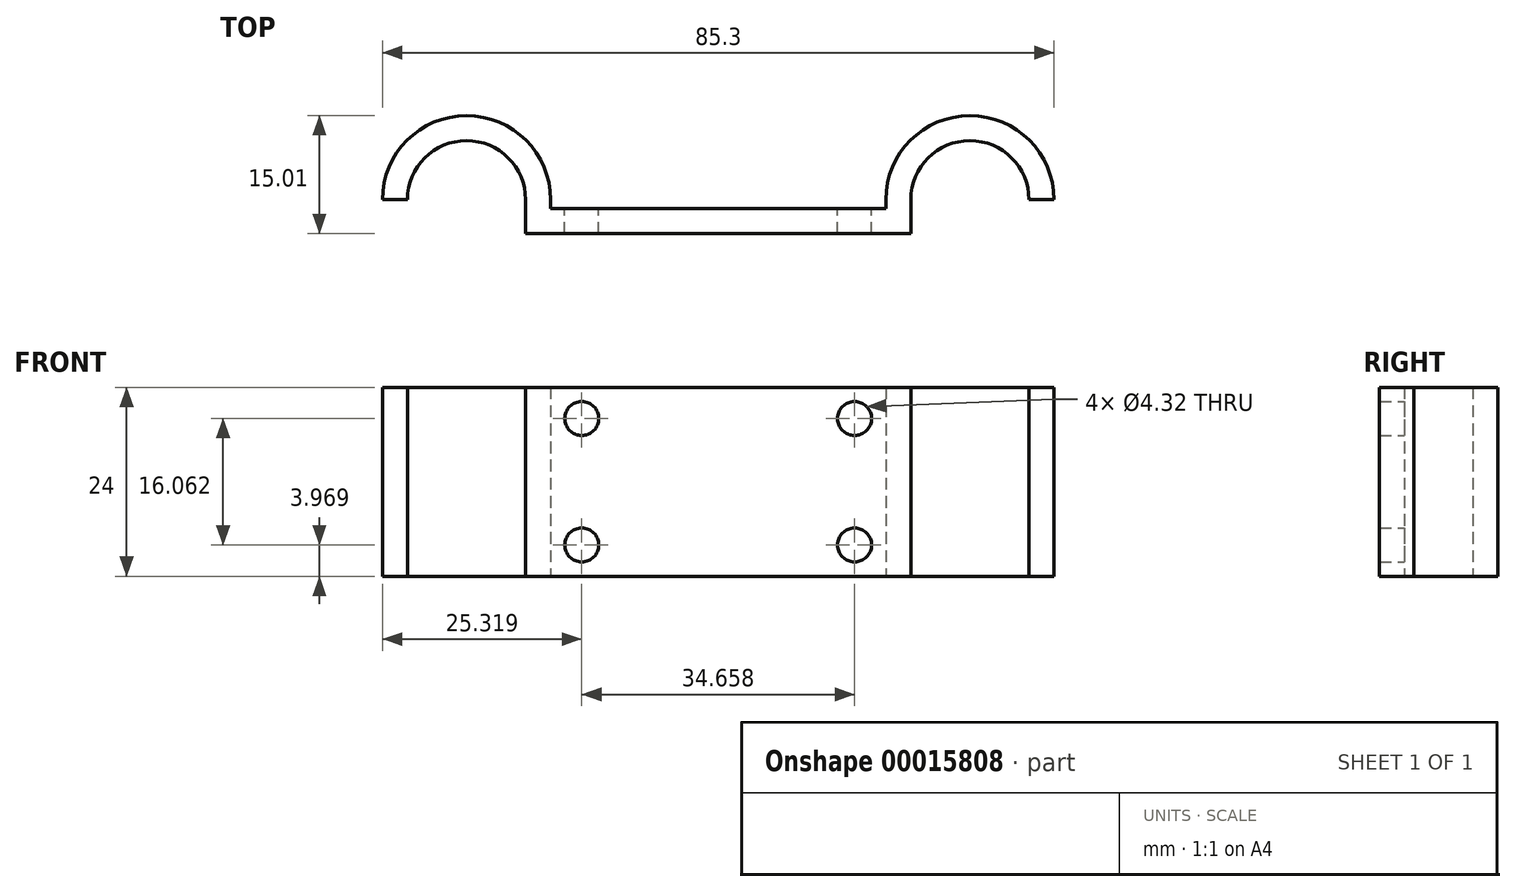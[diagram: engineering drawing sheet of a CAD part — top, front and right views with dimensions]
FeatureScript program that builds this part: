
annotation { "Feature Type Name" : "Feature", "Feature Type Description" : "" }
export const myFeature = defineFeature(function(context is Context, id is Id, definition is map)
    precondition{}
    {
        {
            var Q0;
            Q0=qCreatedBy(makeId("Top.planeOp"),FACE);
            var sketch = newSketch(context, id + "F0", { "sketchPlane" : qUnion([Q0])});
            skLineSegment(sketch, "E0.bottom", {"start": v(0, 0) * mm, "end": v(42.6, 0) * mm});
            skLineSegment(sketch, "E0.top", {"start": v(-3.17, -3.17) * mm, "end": v(45.77, -3.17) * mm});
            skLineSegment(sketch, "E1", {"start": v(21.3, 0) * mm, "end": v(21.3, -3.17) * mm});
            skLineSegment(sketch, "E2", {"start": v(0, 0) * mm, "end": v(0, 1.15) * mm});
            skLineSegment(sketch, "E3", {"start": v(-3.17, -3.17) * mm, "end": v(-3.17, 1.15) * mm});
            skLineSegment(sketch, "E4", {"start": v(42.6, 0) * mm, "end": v(42.6, 1.15) * mm});
            skLineSegment(sketch, "E5", {"start": v(45.77, -3.17) * mm, "end": v(45.77, 1.15) * mm});
            skLineSegment(sketch, "E6", {"start": v(0, 1.15) * mm, "end": v(-3.17, 1.15) * mm});
            skLineSegment(sketch, "E7", {"start": v(42.6, 1.15) * mm, "end": v(45.77, 1.15) * mm});
            skArc(sketch, "E8", {"start": v(-3.18, 1.15) * mm, "mid": v(-10.68, 8.65) * mm, "end": v(-18.18, 1.15) * mm});
            skArc(sketch, "E9", {"start": v(0, 1.15) * mm, "mid": v(-10.67, 11.83) * mm, "end": v(-21.35, 1.15) * mm});
            skArc(sketch, "E10", {"start": v(63.95, 1.15) * mm, "mid": v(53.27, 11.83) * mm, "end": v(42.6, 1.15) * mm});
            skArc(sketch, "E11", {"start": v(60.77, 1.15) * mm, "mid": v(53.27, 8.65) * mm, "end": v(45.77, 1.15) * mm});
            skLineSegment(sketch, "E12", {"start": v(-3.17, 1.15) * mm, "end": v(-18.18, 1.15) * mm, "construction": true});
            skLineSegment(sketch, "E13", {"start": v(-18.17, 1.15) * mm, "end": v(-21.35, 1.15) * mm});
            skLineSegment(sketch, "E14", {"start": v(45.77, 1.15) * mm, "end": v(60.77, 1.15) * mm, "construction": true});
            skLineSegment(sketch, "E15", {"start": v(60.77, 1.15) * mm, "end": v(63.95, 1.15) * mm});
            skSolve(sketch);
        }
        {
            var Q0;
            Q0 = qSketchRegion(id + "F0", true);
            extrude(context, id + "F1", {"entities" : qUnion([Q0]), "depth" : 24 * mm});
        }
        {
            var Q0;
            Q0=makeQuery(id+"F1.opExtrude","SWEPT_FACE",FACE,{"disambiguationData":[OSD([sQuery(id+"F0.wireOp",EDGE,"E0.bottom")])]});
            var sketch = newSketch(context, id + "F2", { "sketchPlane" : qUnion([Q0])});
            skLineSegment(sketch, "E16", {"start": v(-21.3, 0) * mm, "end": v(-21.3, 24) * mm, "construction": true});
            skLineSegment(sketch, "E17.rect.bottom", {"start": v(-38.63, 3.97) * mm, "end": v(-3.97, 3.97) * mm, "construction": true});
            skLineSegment(sketch, "E17.rect.top", {"start": v(-38.63, 20.03) * mm, "end": v(-3.97, 20.03) * mm, "construction": true});
            skLineSegment(sketch, "E17.rect.left", {"start": v(-38.63, 3.97) * mm, "end": v(-38.63, 20.03) * mm, "construction": true});
            skLineSegment(sketch, "E17.rect.right", {"start": v(-3.97, 3.97) * mm, "end": v(-3.97, 20.03) * mm, "construction": true});
            skPoint(sketch, "E17.rect.middle", {"position": v(-21.3, 12) * mm});
            skLineSegment(sketch, "E18.bottom", {"start": v(-38.63, 3.97) * mm, "end": v(-42.6, 3.97) * mm, "construction": true});
            skLineSegment(sketch, "E18.left", {"start": v(-38.63, 3.97) * mm, "end": v(-38.63, 0) * mm, "construction": true});
            skCircle(sketch, "E19", {"center": v(-38.63, 3.97) * mm, "radius": 2.16 * mm});
            skCircle(sketch, "E20", {"center": v(-38.63, 20.03) * mm, "radius": 2.16 * mm});
            skCircle(sketch, "E21", {"center": v(-3.97, 20.03) * mm, "radius": 2.16 * mm});
            skCircle(sketch, "E22", {"center": v(-3.97, 3.97) * mm, "radius": 2.16 * mm});
            skSolve(sketch);
        }
        {
            var Q0;
            Q0 = qSketchRegion(id + "F2", true);
            var Q1;
            Q1=makeQuery(id+"F1.opExtrude","SWEPT_FACE",FACE,{"disambiguationData":[OSD([sQuery(id+"F0.wireOp",EDGE,"E0.top")])]});
            extrude(context, id + "F3", {"entities" : qUnion([Q0]), "operationType" : NewBodyOperationType.REMOVE, "endBound" : BoundingType.UP_TO_SURFACE, "oppositeDirection" : true, "endBoundEntityFace" : qUnion([Q1]), "depth" : 25.4 * mm});
        }
    });
